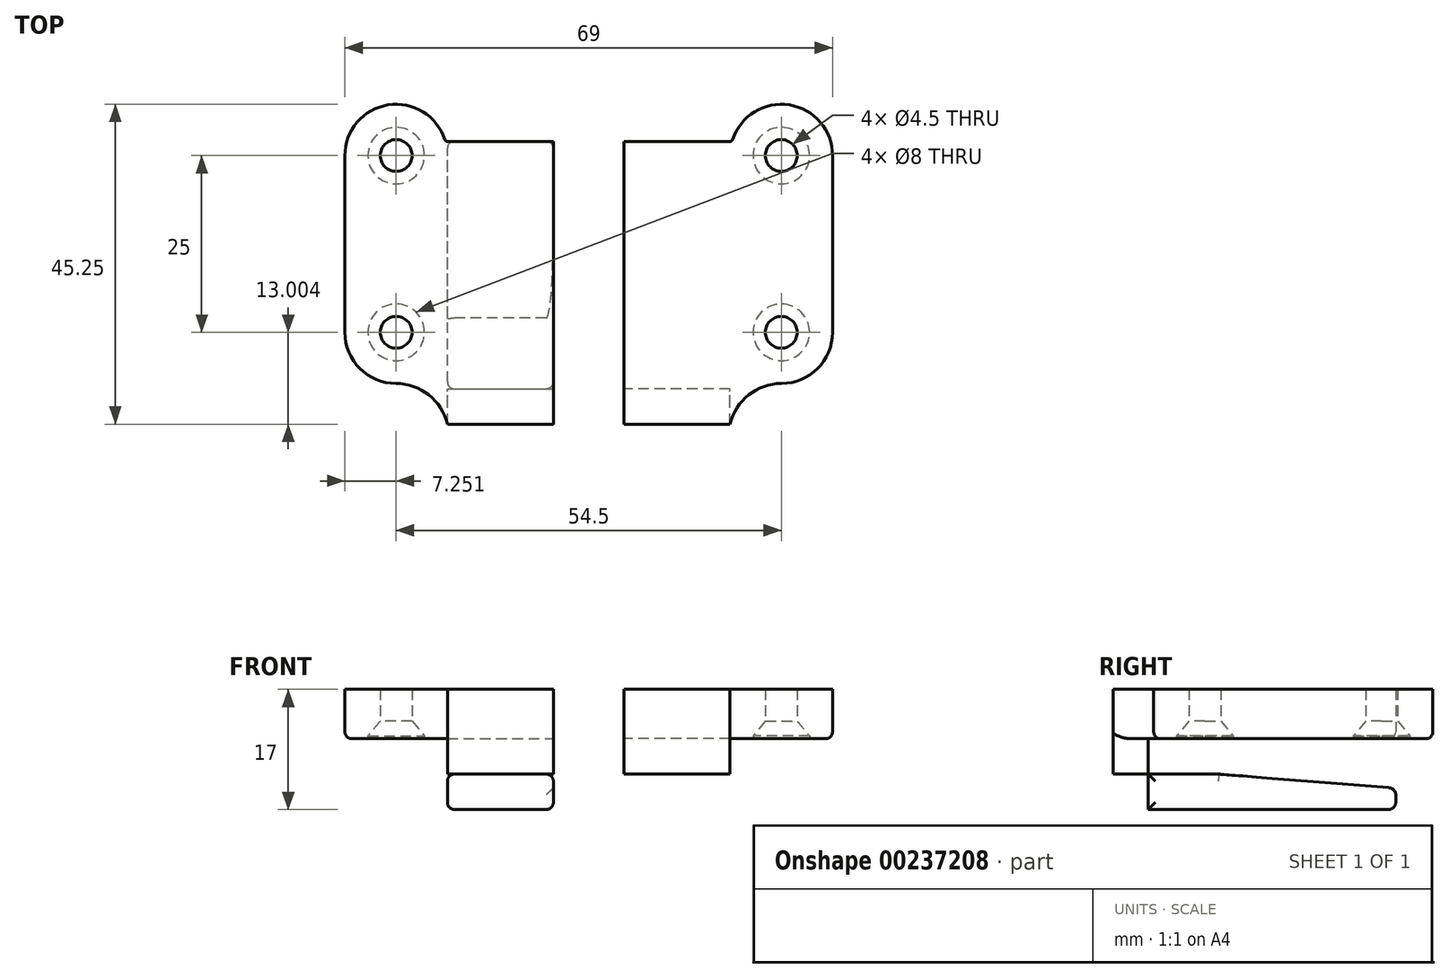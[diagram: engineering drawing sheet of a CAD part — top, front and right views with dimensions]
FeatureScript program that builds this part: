
annotation { "Feature Type Name" : "Feature", "Feature Type Description" : "" }
export const myFeature = defineFeature(function(context is Context, id is Id, definition is map)
    precondition{}
    {
        {
            assignVariable(context, id + "F0", {"name" : "M4_clearance_diameter", "anyValue" : 4.5});
        }
        {
            var Q0;
            Q0=qCreatedBy(makeId("Top.planeOp"),FACE);
            var sketch = newSketch(context, id + "F1", { "sketchPlane" : qUnion([Q0])});
            skCircle(sketch, "E0", {"center": v(-10.53, -5.15) * mm, "radius": 2.25 * mm});
            skLineSegment(sketch, "E1.bottom", {"start": v(-17.78, 27.1) * mm, "end": v(-3.28, 27.1) * mm});
            skLineSegment(sketch, "E1.top", {"start": v(-17.78, -12.4) * mm, "end": v(-3.28, -12.4) * mm});
            skLineSegment(sketch, "E1.left", {"start": v(-17.78, 27.1) * mm, "end": v(-17.78, -12.4) * mm});
            skLineSegment(sketch, "E1.right", {"start": v(-3.28, 27.1) * mm, "end": v(-3.28, -12.4) * mm});
            skCircle(sketch, "E2", {"center": v(-10.53, 19.85) * mm, "radius": 2.25 * mm});
            skCircle(sketch, "E3", {"center": v(-10.53, -5.15) * mm, "radius": 7.25 * mm});
            skCircle(sketch, "E4", {"center": v(-10.53, 19.85) * mm, "radius": 7.25 * mm});
            skSolve(sketch);
        }
        {
            assignVariable(context, id + "F2", {"name" : "hole_depth_psu", "anyValue" : 3});
        }
        {
            assignVariable(context, id + "F3", {"name" : "screw_length", "anyValue" : 7.5});
        }
        {
            assignVariable(context, id + "F4", {"name" : "screw_head_length", "anyValue" : 2.5});
        }
        {
            assignVariable(context, id + "F5", {"name" : "bracket_thickness", "anyValue" : getVariable(context, 'screw_length') + getVariable(context, 'screw_head_length') - getVariable(context, 'hole_depth_psu')});
        }
        {
            var Q0;
            Q0=makeQuery(id+"F1.imprint","IMPRINT",FACE,{"disambiguationData":[TD([[makeQuery(id+"F1.imprint","IMPRINT",EDGE,{"derivedFrom":sQuery(id+"F1.wireOp",EDGE,"E0")}),-1.0]])]});
            var Q1;
            Q1=makeQuery(id+"F1.imprint","IMPRINT",FACE,{"disambiguationData":[TD([[makeQuery(id+"F1.imprint","IMPRINT",EDGE,{"derivedFrom":sQuery(id+"F1.wireOp",EDGE,"E2")}),-1.0]])]});
            var Q2;
            {var subQ0=sQuery(id+"F1.wireOp",EDGE,"E4");var subQ1=sQuery(id+"F1.wireOp",EDGE,"E1.left");var subQ2=makeQuery(id+"F1.imprint","INTERSECT",VERTEX,{"derivedFrom":[subQ1,subQ0]});Q2=makeQuery(id+"F1.imprint","IMPRINT",FACE,{"disambiguationData":[TD([[makeQuery(id+"F1.imprint","IMPRINT",EDGE,{"disambiguationData":[TD([[subQ2,-1.0]])],"derivedFrom":subQ1}),1.0]])]});}
            extrude(context, id + "F6", {"entities" : qUnion([Q0, Q1, Q2]), "depth" : (getVariable(context, 'bracket_thickness')) * mm});
        }
        {
            assignVariable(context, id + "F7", {"name" : "screw_head_diameter", "anyValue" : 8});
        }
        {
            assignVariable(context, id + "F8", {"name" : "screw_head_chamfer", "anyValue" : getVariable(context, 'screw_head_length') - 0.4});
        }
        {
            var Q0;
            Q0=makeQuery(id+"F6.opExtrude","CAP_FACE",FACE,{"disambiguationData":[OSD([sQuery(id+"F1.wireOp",EDGE,"E0"),sQuery(id+"F1.wireOp",EDGE,"E1.bottom"),sQuery(id+"F1.wireOp",EDGE,"E1.left"),sQuery(id+"F1.wireOp",EDGE,"E1.right"),sQuery(id+"F1.wireOp",EDGE,"E2"),sQuery(id+"F1.wireOp",EDGE,"E3")])],"isStart":true});
            var sketch = newSketch(context, id + "F9", { "sketchPlane" : qUnion([Q0])});
            skCircle(sketch, "E5", {"center": v(-10.53, 5.15) * mm, "radius": 4 * mm});
            skCircle(sketch, "E6", {"center": v(-10.53, -19.85) * mm, "radius": 4 * mm});
            skSolve(sketch);
        }
        {
            var Q0;
            Q0=makeQuery(id+"F9.imprint","IMPRINT",FACE,{"disambiguationData":[TD([[makeQuery(id+"F9.imprint","IMPRINT",EDGE,{"derivedFrom":sQuery(id+"F9.wireOp",EDGE,"E5")}),1.0]])]});
            var Q1;
            Q1=makeQuery(id+"F9.imprint","IMPRINT",FACE,{"disambiguationData":[TD([[makeQuery(id+"F9.imprint","IMPRINT",EDGE,{"derivedFrom":sQuery(id+"F9.wireOp",EDGE,"E6")}),1.0]])]});
            extrude(context, id + "F10", {"entities" : qUnion([Q0, Q1]), "operationType" : NewBodyOperationType.REMOVE, "oppositeDirection" : true, "depth" : (getVariable(context, 'screw_head_length')) * mm});
        }
        {
            var Q0;
            Q0=makeQuery(id+"F10.boolean.opBoolean","COPY",EDGE,{"derivedFrom":makeQuery(id+"F10.opExtrude","CAP_EDGE",EDGE,{"disambiguationData":[OSD([sQuery(id+"F9.wireOp",EDGE,"E5")])],"isStart":false})});
            var Q1;
            Q1=makeQuery(id+"F10.boolean.opBoolean","COPY",EDGE,{"derivedFrom":makeQuery(id+"F10.opExtrude","CAP_EDGE",EDGE,{"disambiguationData":[OSD([sQuery(id+"F9.wireOp",EDGE,"E6")])],"isStart":false})});
            chamfer(context, id + "F11", {"entities" : qUnion([Q0, Q1]), "chamferType" : ChamferType.TWO_OFFSETS, "width1" : ((getVariable(context, 'screw_head_diameter') - getVariable(context, 'M4_clearance_diameter')) / 2) * mm, "oppositeDirection" : false, "width2" : (getVariable(context, 'screw_head_chamfer')) * mm, "tangentPropagation" : true});
        }
        {
            var Q0;
            Q0=makeQuery(id+"F6.opExtrude","CAP_FACE",FACE,{"disambiguationData":[OSD([sQuery(id+"F1.wireOp",EDGE,"E0"),sQuery(id+"F1.wireOp",EDGE,"E1.left"),sQuery(id+"F1.wireOp",EDGE,"E1.right"),sQuery(id+"F1.wireOp",EDGE,"E2"),sQuery(id+"F1.wireOp",EDGE,"E3"),sQuery(id+"F1.wireOp",EDGE,"E4")])],"isStart":true});
            var sketch = newSketch(context, id + "F12", { "sketchPlane" : qUnion([Q0])});
            skLineSegment(sketch, "E7.bottom", {"start": v(-3.28, 18.15) * mm, "end": v(11.72, 18.15) * mm});
            skLineSegment(sketch, "E7.top", {"start": v(-3.28, -21.85) * mm, "end": v(11.72, -21.85) * mm});
            skLineSegment(sketch, "E7.left", {"start": v(-3.28, 18.15) * mm, "end": v(-3.28, -21.85) * mm});
            skLineSegment(sketch, "E7.right", {"start": v(11.72, 18.15) * mm, "end": v(11.72, -21.85) * mm});
            skPoint(sketch, "E8", {"position": v(-10.53, 5.15) * mm});
            skArc(sketch, "E9", {"start": v(-10.53, 12.4) * mm, "mid": v(-5.9, 14) * mm, "end": v(-3.28, 18.15) * mm});
            skArc(sketch, "E10", {"start": v(-3.28, -21.85) * mm, "mid": v(-3.5, -21.93) * mm, "end": v(-3.64, -22.12) * mm});
            skSolve(sketch);
        }
        {
            var Q0;
            {var subQ4=sQuery(id+"F12.wireOp",EDGE,"E7.bottom");Q0=makeQuery(id+"F12.imprint","IMPRINT",FACE,{"disambiguationData":[TD([[makeQuery(id+"F12.imprint","IMPRINT",EDGE,{"derivedFrom":subQ4}),-1.0]])]});}
            var Q1;
            {var subQ3=sQuery(id+"F12.wireOp",EDGE,"E9");Q1=makeQuery(id+"F12.imprint","IMPRINT",FACE,{"disambiguationData":[TD([[makeQuery(id+"F12.imprint","IMPRINT",EDGE,{"derivedFrom":subQ3}),-1.0]])]});}
            var Q2;
            {var subQ3=sQuery(id+"F12.wireOp",EDGE,"E10");Q2=makeQuery(id+"F12.imprint","IMPRINT",FACE,{"disambiguationData":[TD([[makeQuery(id+"F12.imprint","IMPRINT",EDGE,{"derivedFrom":subQ3}),-1.0]])]});}
            var Q3;
            Q3=makeQuery(id+"F6.opExtrude","CAP_FACE",FACE,{"disambiguationData":[OSD([sQuery(id+"F1.wireOp",EDGE,"E0"),sQuery(id+"F1.wireOp",EDGE,"E1.left"),sQuery(id+"F1.wireOp",EDGE,"E1.right"),sQuery(id+"F1.wireOp",EDGE,"E2"),sQuery(id+"F1.wireOp",EDGE,"E3"),sQuery(id+"F1.wireOp",EDGE,"E4")])],"isStart":false});
            extrude(context, id + "F13", {"entities" : qUnion([Q0, Q1, Q2]), "operationType" : NewBodyOperationType.ADD, "endBound" : BoundingType.UP_TO_SURFACE, "oppositeDirection" : true, "endBoundEntityFace" : qUnion([Q3]), "depth" : 25 * mm});
        }
        {
            var Q0;
            Q0=makeQuery(id+"F13.opExtrude","SWEPT_FACE",FACE,{"disambiguationData":[OSD([sQuery(id+"F12.wireOp",EDGE,"E7.right")])]});
            var sketch = newSketch(context, id + "F14", { "sketchPlane" : qUnion([Q0])});
            skLineSegment(sketch, "E11.bottom", {"start": v(-18.15, 0) * mm, "end": v(-13.15, 0) * mm});
            skLineSegment(sketch, "E11.top", {"start": v(-18.15, -10) * mm, "end": v(-13.15, -10) * mm});
            skLineSegment(sketch, "E11.left", {"start": v(-18.15, 0) * mm, "end": v(-18.15, -10) * mm});
            skLineSegment(sketch, "E11.right", {"start": v(-13.15, 0) * mm, "end": v(-13.15, -10) * mm});
            skLineSegment(sketch, "E12.bottom", {"start": v(-18.15, -10) * mm, "end": v(21.85, -10) * mm});
            skLineSegment(sketch, "E12.top", {"start": v(-18.15, -5) * mm, "end": v(21.85, -5) * mm});
            skLineSegment(sketch, "E12.left", {"start": v(-18.15, -10) * mm, "end": v(-18.15, -5) * mm});
            skLineSegment(sketch, "E12.right", {"start": v(21.85, -10) * mm, "end": v(21.85, -5) * mm});
            skSolve(sketch);
        }
        {
            var Q0;
            {var subQ5=sQuery(id+"F14.wireOp",EDGE,"E12.right");Q0=makeQuery(id+"F14.imprint","IMPRINT",FACE,{"disambiguationData":[TD([[makeQuery(id+"F14.imprint","IMPRINT",EDGE,{"derivedFrom":subQ5}),1.0]])]});}
            var Q1;
            {var subQ5=sQuery(id+"F14.wireOp",EDGE,"E12.left");Q1=makeQuery(id+"F14.imprint","IMPRINT",FACE,{"disambiguationData":[TD([[makeQuery(id+"F14.imprint","IMPRINT",EDGE,{"derivedFrom":subQ5}),-1.0]])]});}
            var Q2;
            {var subQ0=sQuery(id+"F14.wireOp",EDGE,"E11.bottom");Q2=makeQuery(id+"F14.imprint","IMPRINT",FACE,{"disambiguationData":[TD([[makeQuery(id+"F14.imprint","IMPRINT",EDGE,{"derivedFrom":subQ0}),-1.0]])]});}
            extrude(context, id + "F15", {"entities" : qUnion([Q0, Q1, Q2]), "operationType" : NewBodyOperationType.ADD, "oppositeDirection" : true, "depth" : 15 * mm});
        }
        {
            var Q0;
            Q0=makeQuery(id+"F15.opExtrude","SWEPT_EDGE",EDGE,{"disambiguationData":[OSD([sQuery(id+"F14.wireOp",EDGE,"E12.top"),sQuery(id+"F14.wireOp",EDGE,"E12.right")])]});
            chamfer(context, id + "F16", {"entities" : qUnion([Q0]), "chamferType" : ChamferType.TWO_OFFSETS, "width1" : 2 * mm, "oppositeDirection" : false, "width2" : 25 * mm, "tangentPropagation" : true});
        }
        {
            var Q0;
            Q0=makeQuery(id+"F15.opExtrude","CAP_EDGE",EDGE,{"disambiguationData":[OSD([sQuery(id+"F14.wireOp",EDGE,"E12.bottom")])],"isStart":false});
            var Q1;
            Q1=makeQuery(id+"F15.opExtrude","CAP_EDGE",EDGE,{"disambiguationData":[OSD([sQuery(id+"F14.wireOp",EDGE,"E12.bottom")])],"isStart":true});
            var Q2;
            Q2=makeQuery(id+"F15.opExtrude","CAP_EDGE",EDGE,{"disambiguationData":[OSD([sQuery(id+"F14.wireOp",EDGE,"E12.top")])],"isStart":false});
            var Q3;
            {var subQ0=sQuery(id+"F14.wireOp",EDGE,"E12.right");var subQ1=sQuery(id+"F14.wireOp",EDGE,"E12.top");Q3=makeQuery(id+"F16.opChamfer","BLEND_EDGE",EDGE,{"blendedFrom":[makeQuery(id+"F15.opExtrude","SWEPT_EDGE",EDGE,{"disambiguationData":[OSD([subQ1,subQ0])]}),makeQuery(id+"F15.opExtrude","CAP_FACE",FACE,{"disambiguationData":[OSD([sQuery(id+"F14.wireOp",EDGE,"E11.bottom"),sQuery(id+"F14.wireOp",EDGE,"E11.left"),sQuery(id+"F14.wireOp",EDGE,"E11.right"),sQuery(id+"F14.wireOp",EDGE,"E12.bottom"),subQ1,sQuery(id+"F14.wireOp",EDGE,"E12.left"),subQ0])],"isStart":false})],"blendedInto":[makeQuery(id+"F15.opExtrude","CAP_FACE",FACE,{"disambiguationData":[OSD([sQuery(id+"F14.wireOp",EDGE,"E11.bottom"),sQuery(id+"F14.wireOp",EDGE,"E11.left"),sQuery(id+"F14.wireOp",EDGE,"E11.right"),sQuery(id+"F14.wireOp",EDGE,"E12.bottom"),subQ1,sQuery(id+"F14.wireOp",EDGE,"E12.left"),subQ0])],"isStart":false})]});}
            var Q4;
            {var subQ0=sQuery(id+"F14.wireOp",EDGE,"E12.right");var subQ1=sQuery(id+"F14.wireOp",EDGE,"E12.top");Q4=makeQuery(id+"F16.opChamfer","BLEND_EDGE",EDGE,{"blendedFrom":[makeQuery(id+"F15.opExtrude","SWEPT_EDGE",EDGE,{"disambiguationData":[OSD([subQ1,subQ0])]}),makeQuery(id+"F15.boolean.opBoolean","MERGE",FACE,{"derivedFrom":[makeQuery(id+"F13.opExtrude","SWEPT_FACE",FACE,{"disambiguationData":[OSD([sQuery(id+"F12.wireOp",EDGE,"E7.right")])]}),makeQuery(id+"F15.opExtrude","CAP_FACE",FACE,{"disambiguationData":[OSD([sQuery(id+"F14.wireOp",EDGE,"E11.bottom"),sQuery(id+"F14.wireOp",EDGE,"E11.left"),sQuery(id+"F14.wireOp",EDGE,"E11.right"),sQuery(id+"F14.wireOp",EDGE,"E12.bottom"),subQ1,sQuery(id+"F14.wireOp",EDGE,"E12.left"),subQ0])],"isStart":true})]})],"blendedInto":[makeQuery(id+"F15.boolean.opBoolean","MERGE",FACE,{"derivedFrom":[makeQuery(id+"F13.opExtrude","SWEPT_FACE",FACE,{"disambiguationData":[OSD([sQuery(id+"F12.wireOp",EDGE,"E7.right")])]}),makeQuery(id+"F15.opExtrude","CAP_FACE",FACE,{"disambiguationData":[OSD([sQuery(id+"F14.wireOp",EDGE,"E11.bottom"),sQuery(id+"F14.wireOp",EDGE,"E11.left"),sQuery(id+"F14.wireOp",EDGE,"E11.right"),sQuery(id+"F14.wireOp",EDGE,"E12.bottom"),subQ1,sQuery(id+"F14.wireOp",EDGE,"E12.left"),subQ0])],"isStart":true})]})]});}
            var Q5;
            {var subQ0=sQuery(id+"F14.wireOp",EDGE,"E12.right");Q5=makeQuery(id+"F16.opChamfer","BLEND_EDGE",EDGE,{"blendedFrom":[makeQuery(id+"F15.opExtrude","SWEPT_EDGE",EDGE,{"disambiguationData":[OSD([sQuery(id+"F14.wireOp",EDGE,"E12.top"),subQ0])]}),makeQuery(id+"F15.opExtrude","SWEPT_FACE",FACE,{"disambiguationData":[OSD([subQ0])]})],"blendedInto":[makeQuery(id+"F15.opExtrude","SWEPT_FACE",FACE,{"disambiguationData":[OSD([subQ0])]})]});}
            var Q6;
            Q6=makeQuery(id+"F15.opExtrude","SWEPT_EDGE",EDGE,{"disambiguationData":[OSD([sQuery(id+"F14.wireOp",EDGE,"E12.bottom"),sQuery(id+"F14.wireOp",EDGE,"E12.right")])]});
            var Q7;
            Q7=makeQuery(id+"F15.opExtrude","CAP_EDGE",EDGE,{"disambiguationData":[OSD([sQuery(id+"F14.wireOp",EDGE,"E12.right")])],"isStart":true});
            var Q8;
            Q8=makeQuery(id+"F15.opExtrude","CAP_EDGE",EDGE,{"disambiguationData":[OSD([sQuery(id+"F14.wireOp",EDGE,"E12.right")])],"isStart":false});
            var Q9;
            Q9=makeQuery(id+"F15.opExtrude","CAP_EDGE",EDGE,{"disambiguationData":[OSD([sQuery(id+"F14.wireOp",EDGE,"E11.right")])],"isStart":false});
            var Q10;
            Q10=makeQuery(id+"F15.opExtrude","SWEPT_EDGE",EDGE,{"disambiguationData":[OSD([sQuery(id+"F14.wireOp",EDGE,"E12.bottom"),sQuery(id+"F14.wireOp",EDGE,"E12.left")])]});
            var Q11;
            Q11=makeQuery(id+"F13.opExtrude","SWEPT_EDGE",EDGE,{"disambiguationData":[OSD([sQuery(id+"F12.wireOp",EDGE,"E7.bottom"),sQuery(id+"F12.wireOp",EDGE,"E7.left"),sQuery(id+"F12.wireOp",EDGE,"E9")])]});
            var Q12;
            Q12=makeQuery(id+"F15.opExtrude","CAP_EDGE",EDGE,{"disambiguationData":[OSD([sQuery(id+"F14.wireOp",EDGE,"E12.top")])],"isStart":true});
            var Q13;
            Q13=makeQuery(id+"F15.opExtrude","CAP_EDGE",EDGE,{"disambiguationData":[OSD([sQuery(id+"F14.wireOp",EDGE,"E11.right")])],"isStart":true});
            var Q14;
            Q14=makeQuery(id+"F13.opExtrude","CAP_EDGE",EDGE,{"disambiguationData":[OSD([sQuery(id+"F12.wireOp",EDGE,"E7.right")])],"isStart":true});
            var Q15;
            Q15=makeQuery(id+"F15.boolean.opBoolean","MERGE",EDGE,{"derivedFrom":[makeQuery(id+"F13.opExtrude","SWEPT_EDGE",EDGE,{"disambiguationData":[OSD([sQuery(id+"F12.wireOp",EDGE,"E7.bottom"),sQuery(id+"F12.wireOp",EDGE,"E7.right")])]}),makeQuery(id+"F15.opExtrude","CAP_EDGE",EDGE,{"disambiguationData":[OSD([sQuery(id+"F14.wireOp",EDGE,"E11.left"),sQuery(id+"F14.wireOp",EDGE,"E12.left")])],"isStart":true})]});
            var Q16;
            Q16=makeQuery(id+"F13.opExtrude","SWEPT_EDGE",EDGE,{"disambiguationData":[OSD([sQuery(id+"F12.wireOp",EDGE,"E7.top"),sQuery(id+"F12.wireOp",EDGE,"E7.right")])]});
            var Q17;
            Q17=makeQuery(id+"F13.opExtrude","TWEAK_EDGE",EDGE,{"derivedFrom":[makeQuery(id+"F6.opExtrude","CAP_FACE",FACE,{"disambiguationData":[OSD([sQuery(id+"F1.wireOp",EDGE,"E0"),sQuery(id+"F1.wireOp",EDGE,"E1.left"),sQuery(id+"F1.wireOp",EDGE,"E1.right"),sQuery(id+"F1.wireOp",EDGE,"E2"),sQuery(id+"F1.wireOp",EDGE,"E3"),sQuery(id+"F1.wireOp",EDGE,"E4")])],"isStart":false}),makeQuery(id+"F12.imprint","IMPRINT",EDGE,{"derivedFrom":sQuery(id+"F12.wireOp",EDGE,"E7.right")})]});
            var Q18;
            Q18=makeQuery(id+"F13.opExtrude","TWEAK_EDGE",EDGE,{"derivedFrom":[makeQuery(id+"F6.opExtrude","CAP_FACE",FACE,{"disambiguationData":[OSD([sQuery(id+"F1.wireOp",EDGE,"E0"),sQuery(id+"F1.wireOp",EDGE,"E1.left"),sQuery(id+"F1.wireOp",EDGE,"E1.right"),sQuery(id+"F1.wireOp",EDGE,"E2"),sQuery(id+"F1.wireOp",EDGE,"E3"),sQuery(id+"F1.wireOp",EDGE,"E4")])],"isStart":false}),makeQuery(id+"F12.imprint","IMPRINT",EDGE,{"derivedFrom":sQuery(id+"F12.wireOp",EDGE,"E7.bottom")})]});
            fillet(context, id + "F17", {"entities" : qUnion([Q0, Q1, Q2, Q3, Q4, Q5, Q6, Q7, Q8, Q9, Q10, Q11, Q12, Q13, Q14, Q15, Q16, Q17, Q18]), "radius" : 1 * mm, "tangentPropagation" : true, "allowEdgeOverflow" : false});
        }
        {
            var Q0;
            Q0=makeQuery(id+"F13.opExtrude","CAP_EDGE",EDGE,{"disambiguationData":[OSD([sQuery(id+"F12.wireOp",EDGE,"E7.top")])],"isStart":true});
            var Q1;
            Q1=makeQuery(id+"F13.opExtrude","TWEAK_EDGE",EDGE,{"derivedFrom":[makeQuery(id+"F6.opExtrude","CAP_FACE",FACE,{"disambiguationData":[OSD([sQuery(id+"F1.wireOp",EDGE,"E0"),sQuery(id+"F1.wireOp",EDGE,"E1.left"),sQuery(id+"F1.wireOp",EDGE,"E1.right"),sQuery(id+"F1.wireOp",EDGE,"E2"),sQuery(id+"F1.wireOp",EDGE,"E3"),sQuery(id+"F1.wireOp",EDGE,"E4")])],"isStart":false}),makeQuery(id+"F12.imprint","IMPRINT",EDGE,{"derivedFrom":sQuery(id+"F12.wireOp",EDGE,"E7.top")})]});
            fillet(context, id + "F18", {"entities" : qUnion([Q0, Q1]), "radius" : 1 * mm, "tangentPropagation" : true, "allowEdgeOverflow" : false});
        }
        {
            var Q0;
            Q0=makeQuery(id+"F15.boolean.opBoolean","MERGE",FACE,{"derivedFrom":[makeQuery(id+"F13.opExtrude","SWEPT_FACE",FACE,{"disambiguationData":[OSD([sQuery(id+"F12.wireOp",EDGE,"E7.right")])]}),makeQuery(id+"F15.opExtrude","CAP_FACE",FACE,{"disambiguationData":[OSD([sQuery(id+"F14.wireOp",EDGE,"E11.bottom"),sQuery(id+"F14.wireOp",EDGE,"E11.left"),sQuery(id+"F14.wireOp",EDGE,"E11.right"),sQuery(id+"F14.wireOp",EDGE,"E12.bottom"),sQuery(id+"F14.wireOp",EDGE,"E12.top"),sQuery(id+"F14.wireOp",EDGE,"E12.left"),sQuery(id+"F14.wireOp",EDGE,"E12.right")])],"isStart":true})]});
            cPlane(context, id + "F19", {"entities" : qUnion([Q0]), "cplaneType" : CPlaneType.OFFSET, "offset" : 5 * mm, "width" : 150 * mm, "height" : 150 * mm});
        }
        {
            var Q0;
            Q0=makeQuery(id+"F6.opExtrude","SWEPT_BODY",BODY,{"disambiguationData":[OSD([sQuery(id+"F1.wireOp",EDGE,"E0"),sQuery(id+"F1.wireOp",EDGE,"E1.left"),sQuery(id+"F1.wireOp",EDGE,"E1.right"),sQuery(id+"F1.wireOp",EDGE,"E2"),sQuery(id+"F1.wireOp",EDGE,"E3"),sQuery(id+"F1.wireOp",EDGE,"E4")])]});
            var Q1;
            Q1=qCreatedBy(id+"F19.planeOp",FACE);
            mirror(context, id + "F20", {"entities" : qUnion([Q0]), "mirrorPlane" : qUnion([Q1])});
        }
    });
